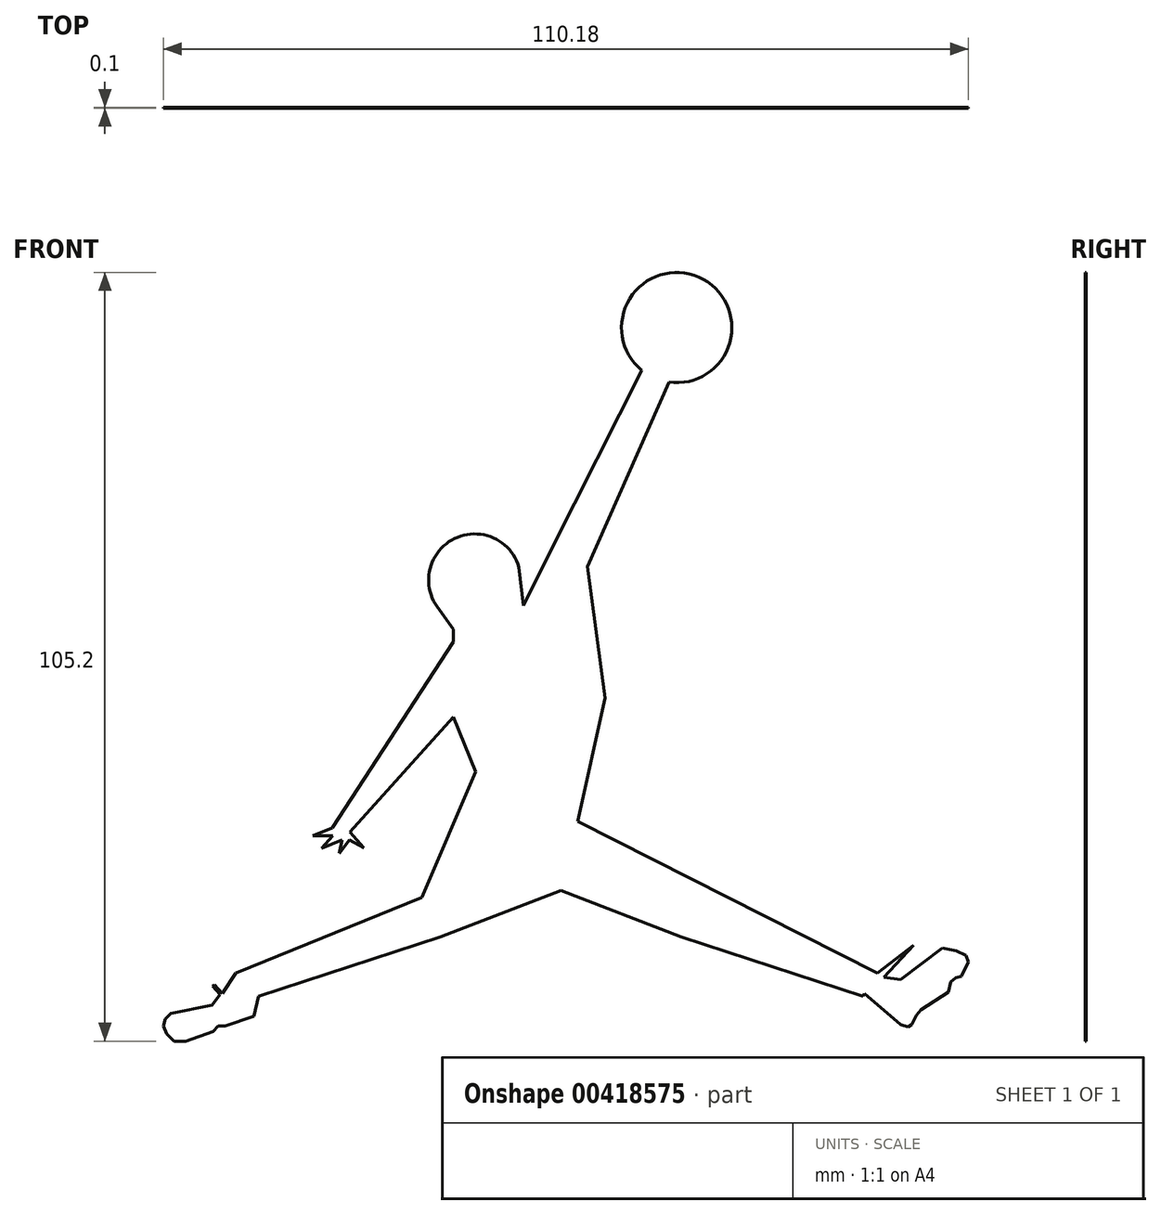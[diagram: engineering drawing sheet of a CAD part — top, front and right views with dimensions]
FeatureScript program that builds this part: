
annotation { "Feature Type Name" : "Feature", "Feature Type Description" : "" }
export const myFeature = defineFeature(function(context is Context, id is Id, definition is map)
    precondition{}
    {
        {
            var Q0;
            Q0=qCreatedBy(makeId("Front.planeOp"),FACE);
            var sketch = newSketch(context, id + "F0", { "sketchPlane" : qUnion([Q0])});
            skArc(sketch, "E0", {"start": v(-16.48, 70.15) * mm, "mid": v(-12.37, 84.53) * mm, "end": v(-20.2, 71.78) * mm});
            skLineSegment(sketch, "E1", {"start": v(-20.2, 71.78) * mm, "end": v(-32.46, 47.52) * mm});
            skLineSegment(sketch, "E2", {"start": v(-16.48, 70.15) * mm, "end": v(-27.6, 44.9) * mm});
            skLineSegment(sketch, "E3", {"start": v(-27.6, 44.9) * mm, "end": v(-25.2, 26.95) * mm});
            skLineSegment(sketch, "E4", {"start": v(-25.2, 26.95) * mm, "end": v(-28.97, 10.02) * mm});
            skLineSegment(sketch, "E5", {"start": v(-28.97, 10.02) * mm, "end": v(12.05, -10.71) * mm});
            skLineSegment(sketch, "E6", {"start": v(12.05, -10.71) * mm, "end": v(17.03, -6.9) * mm});
            skLineSegment(sketch, "E7", {"start": v(17.03, -6.9) * mm, "end": v(12.96, -11.3) * mm});
            skLineSegment(sketch, "E8", {"start": v(12.96, -11.3) * mm, "end": v(15.26, -11.63) * mm});
            skLineSegment(sketch, "E9", {"start": v(15.26, -11.63) * mm, "end": v(20.95, -7.3) * mm});
            skLineSegment(sketch, "E10", {"start": v(20.95, -7.3) * mm, "end": v(22.84, -7.67) * mm});
            skLineSegment(sketch, "E11", {"start": v(22.84, -7.67) * mm, "end": v(24.19, -8.35) * mm});
            skLineSegment(sketch, "E12", {"start": v(24.19, -8.35) * mm, "end": v(24.5, -9.23) * mm});
            skLineSegment(sketch, "E13", {"start": v(24.5, -9.23) * mm, "end": v(23.53, -11.16) * mm});
            skLineSegment(sketch, "E14", {"start": v(23.53, -11.16) * mm, "end": v(22.8, -11.39) * mm});
            skLineSegment(sketch, "E15", {"start": v(22.8, -11.39) * mm, "end": v(22.08, -11.94) * mm});
            skLineSegment(sketch, "E16", {"start": v(22.08, -11.94) * mm, "end": v(21.79, -13.34) * mm});
            skLineSegment(sketch, "E17", {"start": v(21.79, -13.34) * mm, "end": v(18.01, -15.77) * mm});
            skLineSegment(sketch, "E18", {"start": v(18.01, -15.77) * mm, "end": v(17.38, -16.5) * mm});
            skLineSegment(sketch, "E19", {"start": v(17.38, -16.5) * mm, "end": v(16.75, -17.76) * mm});
            skLineSegment(sketch, "E20", {"start": v(16.75, -17.76) * mm, "end": v(16.26, -18.07) * mm});
            skLineSegment(sketch, "E21", {"start": v(16.26, -18.07) * mm, "end": v(15.26, -17.76) * mm});
            skLineSegment(sketch, "E22", {"start": v(15.26, -17.76) * mm, "end": v(10.29, -13.53) * mm});
            skLineSegment(sketch, "E23", {"start": v(10.29, -13.53) * mm, "end": v(10.1, -13.9) * mm});
            skLineSegment(sketch, "E24", {"start": v(10.1, -13.9) * mm, "end": v(-14.8, -5.77) * mm});
            skLineSegment(sketch, "E25", {"start": v(-14.8, -5.77) * mm, "end": v(-31.27, 0.58) * mm});
            skLineSegment(sketch, "E26.MirrorCS", {"start": v(-47.73, -5.77) * mm, "end": v(-31.27, 0.58) * mm});
            skLineSegment(sketch, "E27.MirrorCS", {"start": v(-72.63, -13.9) * mm, "end": v(-47.73, -5.77) * mm});
            skLineSegment(sketch, "E28", {"start": v(-72.63, -13.9) * mm, "end": v(-73.3, -16.65) * mm});
            skLineSegment(sketch, "E29", {"start": v(-73.3, -16.65) * mm, "end": v(-77.23, -18) * mm});
            skLineSegment(sketch, "E30", {"start": v(-77.23, -18) * mm, "end": v(-78.14, -18) * mm});
            skLineSegment(sketch, "E31", {"start": v(-78.14, -18) * mm, "end": v(-78.87, -18.74) * mm});
            skLineSegment(sketch, "E32", {"start": v(-78.87, -18.74) * mm, "end": v(-82.6, -20.04) * mm});
            skLineSegment(sketch, "E33", {"start": v(-82.6, -20.04) * mm, "end": v(-84.2, -20.04) * mm});
            skLineSegment(sketch, "E34", {"start": v(-84.2, -20.04) * mm, "end": v(-85.25, -19.08) * mm});
            skLineSegment(sketch, "E35", {"start": v(-85.25, -19.08) * mm, "end": v(-85.67, -18) * mm});
            skLineSegment(sketch, "E36", {"start": v(-85.67, -18) * mm, "end": v(-85.4, -17) * mm});
            skLineSegment(sketch, "E37", {"start": v(-85.4, -17) * mm, "end": v(-84.66, -16.28) * mm});
            skLineSegment(sketch, "E38", {"start": v(-84.66, -16.28) * mm, "end": v(-79, -15.1) * mm});
            skLineSegment(sketch, "E39", {"start": v(-79, -15.1) * mm, "end": v(-77.92, -13.65) * mm});
            skLineSegment(sketch, "E40", {"start": v(-77.92, -13.65) * mm, "end": v(-78.93, -12.52) * mm});
            skLineSegment(sketch, "E41", {"start": v(-78.93, -12.52) * mm, "end": v(-78.69, -12.3) * mm});
            skLineSegment(sketch, "E42", {"start": v(-78.69, -12.3) * mm, "end": v(-77.6, -13.5) * mm});
            skLineSegment(sketch, "E43", {"start": v(-77.6, -13.5) * mm, "end": v(-75.78, -10.76) * mm});
            skLineSegment(sketch, "E44", {"start": v(-75.78, -10.76) * mm, "end": v(-50.28, -0.35) * mm});
            skLineSegment(sketch, "E45", {"start": v(-50.28, -0.35) * mm, "end": v(-42.93, 16.81) * mm});
            skLineSegment(sketch, "E46", {"start": v(-42.93, 16.81) * mm, "end": v(-46, 24.32) * mm});
            skLineSegment(sketch, "E47", {"start": v(-46, 24.32) * mm, "end": v(-60.15, 8.56) * mm});
            skLineSegment(sketch, "E48", {"start": v(-60.15, 8.56) * mm, "end": v(-58.22, 6.42) * mm});
            skLineSegment(sketch, "E49", {"start": v(-58.22, 6.42) * mm, "end": v(-60.23, 7.48) * mm});
            skLineSegment(sketch, "E50", {"start": v(-60.23, 7.48) * mm, "end": v(-61.59, 5.67) * mm});
            skLineSegment(sketch, "E51", {"start": v(-61.59, 5.67) * mm, "end": v(-61.24, 7.48) * mm});
            skLineSegment(sketch, "E52", {"start": v(-61.24, 7.48) * mm, "end": v(-64.02, 6.35) * mm});
            skLineSegment(sketch, "E53", {"start": v(-64.02, 6.35) * mm, "end": v(-62.5, 8.05) * mm});
            skLineSegment(sketch, "E54", {"start": v(-62.5, 8.05) * mm, "end": v(-65.22, 8.05) * mm});
            skLineSegment(sketch, "E55", {"start": v(-65.22, 8.05) * mm, "end": v(-62.53, 9.14) * mm});
            skLineSegment(sketch, "E56", {"start": v(-62.53, 9.14) * mm, "end": v(-46, 34.63) * mm});
            skLineSegment(sketch, "E57", {"start": v(-46, 34.63) * mm, "end": v(-46, 36.3) * mm});
            skArc(sketch, "E58", {"start": v(-37, 44.85) * mm, "mid": v(-45.81, 48.74) * mm, "end": v(-48.2, 39.42) * mm});
            skLineSegment(sketch, "E59", {"start": v(-46, 36.3) * mm, "end": v(-48.2, 39.42) * mm});
            skLineSegment(sketch, "E60", {"start": v(-37, 44.85) * mm, "end": v(-36.4, 39.59) * mm});
            skLineSegment(sketch, "E61", {"start": v(-36.4, 39.59) * mm, "end": v(-32.46, 47.52) * mm});
            skSolve(sketch);
        }
        {
            var Q0;
            Q0 = qSketchRegion(id + "F0", true);
            extrude(context, id + "F1", {"entities" : qUnion([Q0]), "depth" : 0.1 * mm});
        }
    });
